# Revit family: Storage-Teknion-EMMP_Mini_Cabinet_on_Casters-R2016
name_source: partatom
category: Furniture
revit_build: Autodesk Revit 2018 (Build: 20190510_1515(x64)
units: mm (PartAtom-declared; Revit-internal decimal feet)

## family parameters
Always vertical = Yes
Cut with Voids When Loaded = No
OmniClass Number = 23.40.20.00
OmniClass Title = General Furniture and Specialties
Room Calculation Point = No
Shared = Yes
Work Plane-Based = No

## types (4) — shared parameters
Assembly Code = E2020200
Manufacturer = Teknion
Manufacturer Fax = 416.661.4586
Part Number = EMMP
Product Documentation Link = https://assets.teknion.com
Product Line = Emote
Product Page URL = https://www.teknion.com
Series = Emote
Sustainability Data = https://www.teknion.com
URL = www.teknion.com
Unit Weight URL = http://www.teknion.com
Warranty = http://www.teknion.com

## per-type parameters (varying)
| type | Description | Door Visibility | Model | Open | Single Door | Single Door Left Handedness | Single Door Right Handedness |
| Open Storage Configuration | Mini Cabinet on Casters, Open Storage Configuration, 15" Width, 16.69" Depth, 22" Height | No | EMMPOP151622 | Yes | No | No | No |
| Single Door, Left Handedness | Mini Cabinet on Casters, Single Door Left Handedness Storage Configuration, 15" Width, 16.69" Depth, 22" Height | Yes | EMMPLC151622 | No | Yes | Yes | No |
| Single Door, Right Handedness | Mini Cabinet on Casters, Single Door Right Handedness Storage Configuration, 15" Width, 16.69" Depth, 22" Height | Yes | EMMPRC151622 | No | Yes | No | Yes |
| Small Drawer | Mini Cabinet on Casters, Small Drawer Storage Configuration, 15" Width, 16.69" Depth, 22" Height | Yes | EMMPSD151622 | No | Yes | No | No |

type visibility flags (boolean, named after types; folded from table):
- Open Storage Configuration: Yes: (none)
- Single Door, Left Handedness: Yes: (none)
- Single Door, Right Handedness: Yes: (none)
- Small Drawer: Yes: Small Drawer

## geometry (parser evidence)
native form markers: Blend x47, Sweep x2
no freeform markers — native parametric forms only
